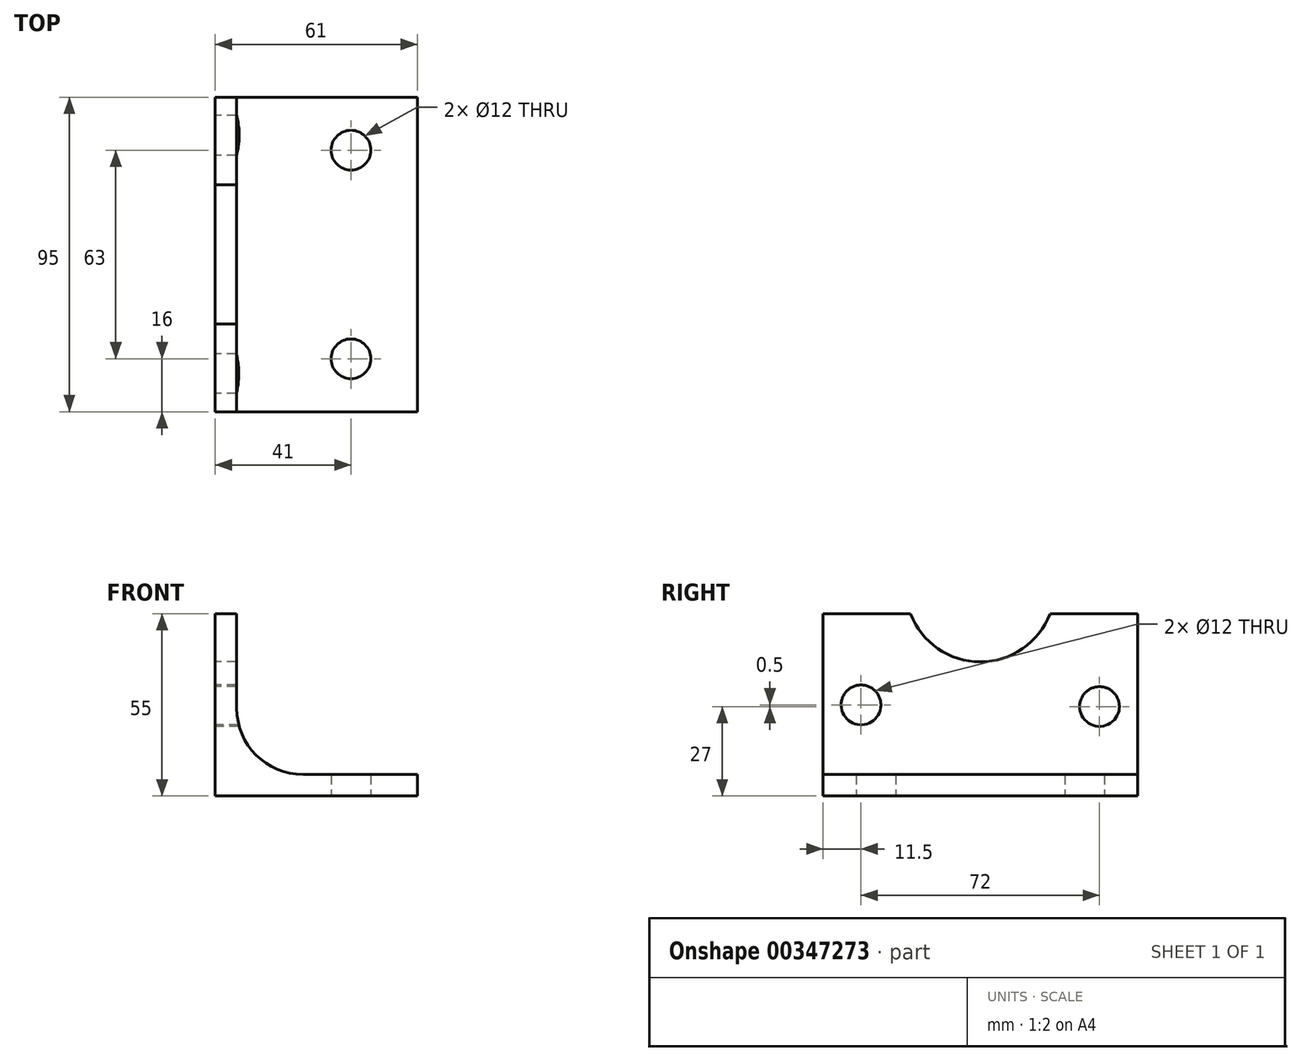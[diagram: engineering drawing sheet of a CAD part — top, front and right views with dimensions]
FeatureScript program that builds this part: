
annotation { "Feature Type Name" : "Feature", "Feature Type Description" : "" }
export const myFeature = defineFeature(function(context is Context, id is Id, definition is map)
    precondition{}
    {
        {
            var Q0;
            Q0=qCreatedBy(makeId("Front.planeOp"),FACE);
            var sketch = newSketch(context, id + "F0", { "sketchPlane" : qUnion([Q0])});
            skLineSegment(sketch, "E0", {"start": v(0, 0) * mm, "end": v(61, 0) * mm});
            skLineSegment(sketch, "E1", {"start": v(61, 0) * mm, "end": v(61, 6.5) * mm});
            skLineSegment(sketch, "E2", {"start": v(61, 6.5) * mm, "end": v(26.5, 6.5) * mm});
            skLineSegment(sketch, "E3", {"start": v(6.5, 26.5) * mm, "end": v(6.5, 55) * mm});
            skLineSegment(sketch, "E4", {"start": v(6.5, 55) * mm, "end": v(0, 55) * mm});
            skLineSegment(sketch, "E5", {"start": v(0, 55) * mm, "end": v(0, 0) * mm});
            skPoint(sketch, "E6.visualSharp", {"position": v(6.5, 6.5) * mm});
            skArc(sketch, "E6.filletArc", {"start": v(6.5, 26.5) * mm, "mid": v(12.36, 12.36) * mm, "end": v(26.5, 6.5) * mm});
            skSolve(sketch);
        }
        {
            var Q0;
            Q0=makeQuery(id+"F0.imprint","IMPRINT",FACE,{"disambiguationData":[TD([[makeQuery(id+"F0.imprint","IMPRINT",EDGE,{"derivedFrom":sQuery(id+"F0.wireOp",EDGE,"E0")}),1.0]])]});
            extrude(context, id + "F1", {"entities" : qUnion([Q0]), "endBound" : BoundingType.SYMMETRIC, "depth" : 95 * mm});
        }
        {
            var Q0;
            Q0=makeQuery(id+"F1.opExtrude","SWEPT_FACE",FACE,{"disambiguationData":[OSD([sQuery(id+"F0.wireOp",EDGE,"E0")])]});
            var sketch = newSketch(context, id + "F2", { "sketchPlane" : qUnion([Q0])});
            skLineSegment(sketch, "E7.0", {"start": v(41, 47.5) * mm, "end": v(41, -47.5) * mm, "construction": true});
            skLineSegment(sketch, "E8.0", {"start": v(0, 31.5) * mm, "end": v(61, 31.5) * mm, "construction": true});
            skLineSegment(sketch, "E9.0", {"start": v(0, -31.5) * mm, "end": v(61, -31.5) * mm, "construction": true});
            skCircle(sketch, "E10", {"center": v(41, 31.5) * mm, "radius": 6 * mm});
            skCircle(sketch, "E11", {"center": v(41, -31.5) * mm, "radius": 6 * mm});
            skSolve(sketch);
        }
        {
            var Q0;
            Q0=makeQuery(id+"F2.imprint","IMPRINT",FACE,{"disambiguationData":[TD([[makeQuery(id+"F2.imprint","IMPRINT",EDGE,{"derivedFrom":sQuery(id+"F2.wireOp",EDGE,"E10")}),1.0]])]});
            var Q1;
            Q1=makeQuery(id+"F2.imprint","IMPRINT",FACE,{"disambiguationData":[TD([[makeQuery(id+"F2.imprint","IMPRINT",EDGE,{"derivedFrom":sQuery(id+"F2.wireOp",EDGE,"E11")}),1.0]])]});
            extrude(context, id + "F3", {"entities" : qUnion([Q0, Q1]), "operationType" : NewBodyOperationType.REMOVE, "endBound" : BoundingType.THROUGH_ALL, "oppositeDirection" : true, "depth" : 25 * mm});
        }
        {
            var Q0;
            Q0=makeQuery(id+"F1.opExtrude","SWEPT_FACE",FACE,{"disambiguationData":[OSD([sQuery(id+"F0.wireOp",EDGE,"E5")])]});
            var sketch = newSketch(context, id + "F4", { "sketchPlane" : qUnion([Q0])});
            skLineSegment(sketch, "E12.0", {"start": v(47.5, 55) * mm, "end": v(-47.5, 55) * mm, "construction": true});
            skLineSegment(sketch, "E13.0", {"start": v(-47.5, 55) * mm, "end": v(-47.5, 0) * mm, "construction": true});
            skLineSegment(sketch, "E14.0", {"start": v(47.5, 55) * mm, "end": v(47.5, 0) * mm, "construction": true});
            skLineSegment(sketch, "E15.0", {"start": v(-36, 55) * mm, "end": v(-36, 0) * mm, "construction": true});
            skLineSegment(sketch, "E16.0", {"start": v(36, 55) * mm, "end": v(36, 0) * mm, "construction": true});
            skLineSegment(sketch, "E17", {"start": v(-56.18, 63) * mm, "end": v(53.5, 63) * mm, "construction": true});
            skCircle(sketch, "E18", {"center": v(0, 63) * mm, "radius": 22.5 * mm});
            skLineSegment(sketch, "E19.0", {"start": v(-56.18, 27) * mm, "end": v(53.5, 27) * mm, "construction": true});
            skCircle(sketch, "E20", {"center": v(-36, 27) * mm, "radius": 6 * mm});
            skCircle(sketch, "E21", {"center": v(36, 27.5) * mm, "radius": 6 * mm});
            skSolve(sketch);
        }
        {
            var Q0;
            Q0=makeQuery(id+"F4.imprint","IMPRINT",FACE,{"disambiguationData":[TD([[makeQuery(id+"F4.imprint","IMPRINT",EDGE,{"derivedFrom":sQuery(id+"F4.wireOp",EDGE,"E20")}),1.0]])]});
            var Q1;
            Q1=makeQuery(id+"F4.imprint","IMPRINT",FACE,{"disambiguationData":[TD([[makeQuery(id+"F4.imprint","IMPRINT",EDGE,{"derivedFrom":sQuery(id+"F4.wireOp",EDGE,"E21")}),1.0]])]});
            var Q2;
            {var subQ0=sQuery(id+"F4.wireOp",EDGE,"E18");var subQ1=makeQuery(id+"F1.opExtrude","SWEPT_EDGE",EDGE,{"disambiguationData":[OSD([sQuery(id+"F0.wireOp",EDGE,"E4"),sQuery(id+"F0.wireOp",EDGE,"E5")])]});var subQ2=makeQuery(id+"F4.imprint","INTERSECT",VERTEX,{"disambiguationData":[OD(0.0)],"derivedFrom":[subQ1,subQ0]});Q2=makeQuery(id+"F4.imprint","IMPRINT",FACE,{"disambiguationData":[TD([[makeQuery(id+"F4.imprint","IMPRINT",EDGE,{"disambiguationData":[TD([[subQ2,-1.0]])],"derivedFrom":subQ0}),1.0]])]});}
            extrude(context, id + "F5", {"entities" : qUnion([Q0, Q1, Q2]), "operationType" : NewBodyOperationType.REMOVE, "endBound" : BoundingType.THROUGH_ALL, "oppositeDirection" : true, "depth" : 25 * mm});
        }
    });
